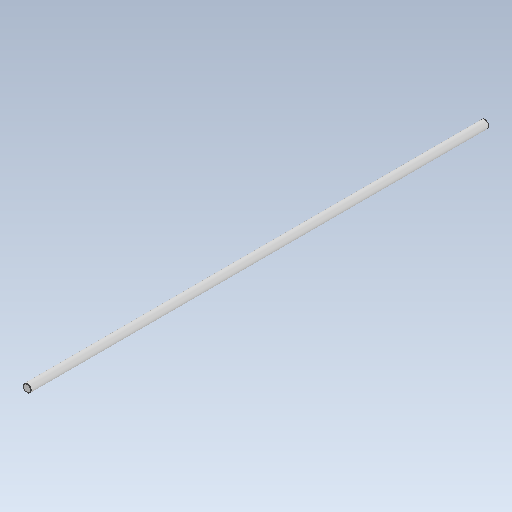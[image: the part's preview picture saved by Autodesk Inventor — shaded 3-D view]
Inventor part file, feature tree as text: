
AUTODESK INVENTOR PART (.ipt)
format: ipt  version: 2020 (Build 240168000, 168)  size: 86,016 bytes
history: native  units: mm
features: extrude x1, chamfer x1, sketch x1
ambient origin geometry x8: Origin, YZ Plane, XZ Plane, XY Plane, X Axis, Y Axis, Z Axis, Center Point
bodies: Solid1 (feature_tree)
feature tree (3):
  extrude  "Extrusion1"  Depth=568.0mm TaperAngle=0.0deg
  chamfer  "Chamfer1"  Distance=0.5mm Angle=45.0deg
  sketch  "Sketch1"  dims[d0=10.0mm d1=568.0mm d2=0.0mm d3=0.5mm d4=2.0mm d5=45.0deg]
